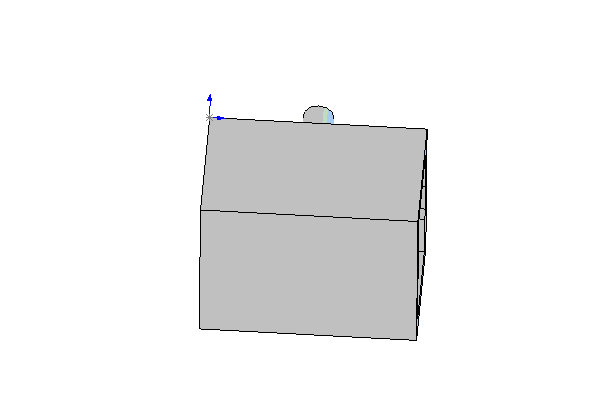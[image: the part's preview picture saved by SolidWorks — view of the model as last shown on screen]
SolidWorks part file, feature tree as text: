
SOLIDWORKS PART (.sldprt)
format: sldprt  version: not decoded by parser v0  size: 99,840 bytes
history: native  units: mm
features: sketch x3, extrude x2, material x1, cut_extrude x1 (+13 scaffold rows collapsed)
feature tree (20):
  scaffold x13  (default folders/planes/origin — collapsed)
  material  "Material <not specified>"
  sketch  "Sketch1"  dims[D1=21.06mm D2=15.8mm]
  extrude  "Extrude1"  Depth=13.06mm
  sketch  "Sketch2"  dims[D1=3.0mm D2=3.0mm D3=10.72mm D4=10.72mm D5=11.43mm D6=2.12mm]
  extrude  "Extrude2"  Depth=3.25mm
  sketch  "Sketch3"
  cut_extrude  "Cut-Extrude1"  Depth=18mm
decode coverage: 5 of 6 modeling features carry decoded parameters
note: suppression state not decoded; provenance and decode notes live in map.json
